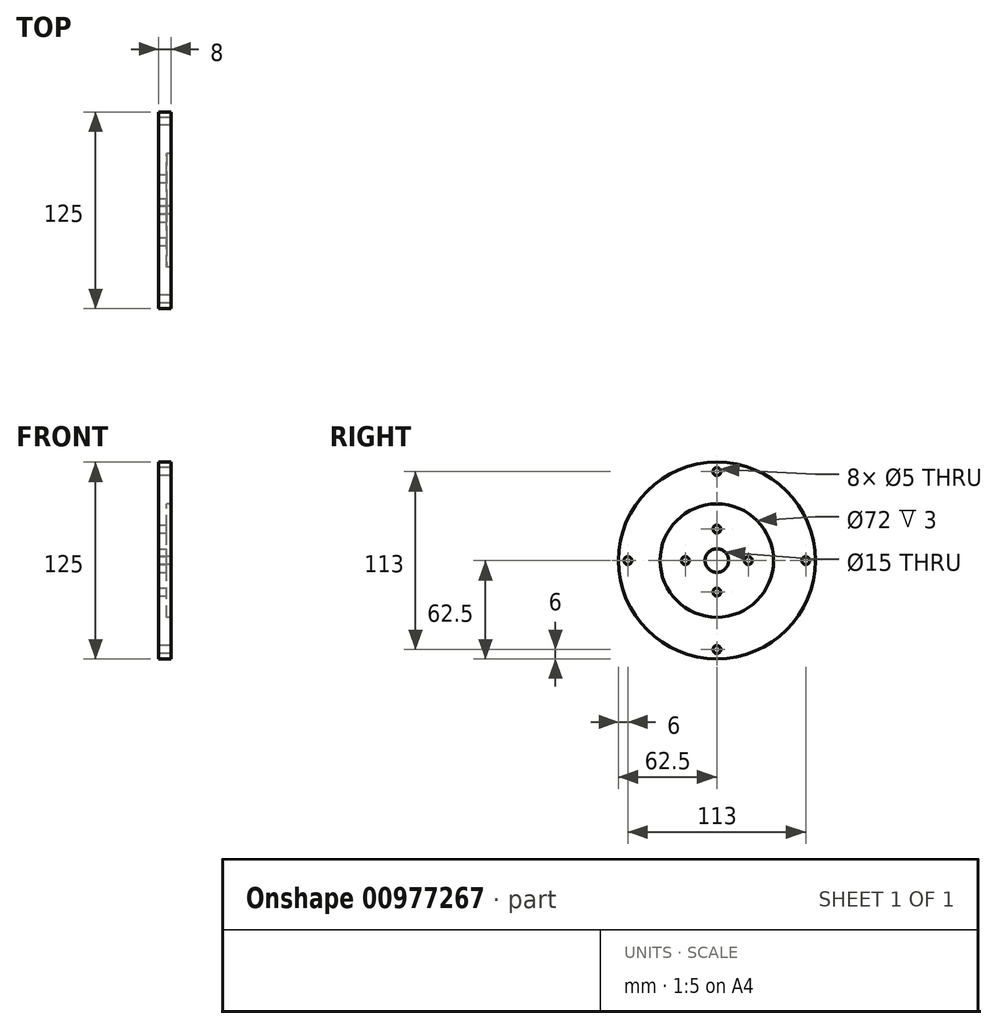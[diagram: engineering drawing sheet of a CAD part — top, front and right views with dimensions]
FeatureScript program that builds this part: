
annotation { "Feature Type Name" : "Feature", "Feature Type Description" : "" }
export const myFeature = defineFeature(function(context is Context, id is Id, definition is map)
    precondition{}
    {
        {
            var Q0;
            Q0=qCreatedBy(makeId("Right.planeOp"),FACE);
            var sketch = newSketch(context, id + "F0", { "sketchPlane" : qUnion([Q0])});
            skCircle(sketch, "E0", {"center": v(0, 0) * mm, "radius": 36 * mm});
            skCircle(sketch, "E1", {"center": v(0, 0) * mm, "radius": 62.5 * mm});
            skCircle(sketch, "E2", {"center": v(0, 56.5) * mm, "radius": 2.5 * mm});
            skCircle(sketch, "E3", {"center": v(56.5, 0) * mm, "radius": 2.5 * mm});
            skCircle(sketch, "E4", {"center": v(0, -56.5) * mm, "radius": 2.5 * mm});
            skCircle(sketch, "E5", {"center": v(-56.5, 0) * mm, "radius": 2.5 * mm});
            skCircle(sketch, "E6", {"center": v(0, 0) * mm, "radius": 7.5 * mm});
            skCircle(sketch, "E7", {"center": v(20, 0) * mm, "radius": 2.5 * mm});
            skCircle(sketch, "E8", {"center": v(0, 20) * mm, "radius": 2.5 * mm});
            skCircle(sketch, "E9", {"center": v(-20, 0) * mm, "radius": 2.5 * mm});
            skCircle(sketch, "E10", {"center": v(0, -20) * mm, "radius": 2.5 * mm});
            skSolve(sketch);
        }
        {
            var Q0;
            Q0=qSketchRegion(id+"F0",true);
            extrude(context, id + "F1", {"entities" : qUnion([Q0]), "depth" : 3 * mm, "offsetDistance" : 25 * mm});
        }
        {
            var Q0;
            Q0=makeQuery(id+"F0.imprint","IMPRINT",FACE,{"disambiguationData":[TD([[makeQuery(id+"F0.imprint","IMPRINT",EDGE,{"derivedFrom":sQuery(id+"F0.wireOp",EDGE,"E0")}),-1.0]])]});
            var Q1;
            Q1=makeQuery(id+"F0.imprint","IMPRINT",FACE,{"disambiguationData":[TD([[makeQuery(id+"F0.imprint","IMPRINT",EDGE,{"derivedFrom":sQuery(id+"F0.wireOp",EDGE,"E0")}),1.0]])]});
            extrude(context, id + "F2", {"entities" : qUnion([Q0, Q1]), "operationType" : NewBodyOperationType.ADD, "oppositeDirection" : true, "depth" : 5 * mm, "offsetDistance" : 25 * mm});
        }
    });
